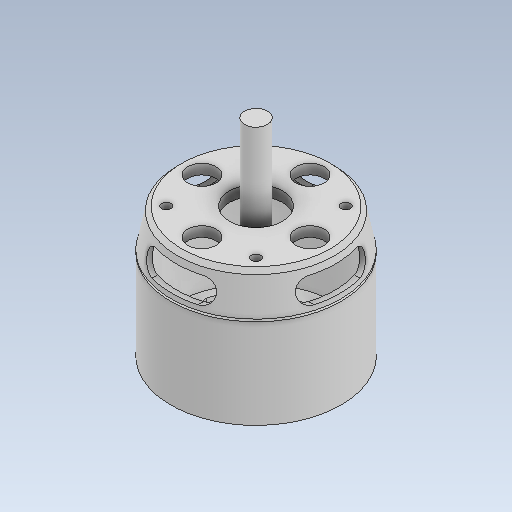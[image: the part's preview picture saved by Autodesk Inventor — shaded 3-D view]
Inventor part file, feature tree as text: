
AUTODESK INVENTOR PART (.ipt)
format: ipt  version: 2023 (Build 270158000, 158)  size: 352,768 bytes
history: native  units: in
note: dims shown in document units (in); Inventor stores cm internally (conversion verified against a paired STEP export)
features: extrude x4, sketch x4, pattern_circular x2, revolve x1, plane x1
ambient origin geometry x8: Origin, YZ Plane, XZ Plane, XY Plane, X Axis, Y Axis, Z Axis, Center Point
bodies: Solid1 (feature_tree)
feature tree (12):
  revolve  "Revolution1"  [1 undecoded]
  extrude  "Extrusion1"  Depth=0.5161in
  plane  "Work Plane1"
  extrude  "Extrusion2"  Depth=0.0787in
  sketch  "Sketch4"  dims[d6=45.0deg d7=0.3616in d8=0.0315in d9=1.2252in d10=0.1102in d11=0.1575in d12=3.2677in d13=1.0433in d14=0.0835in d16=0.0709in d17=0.1102in d18=0.3248in d19=0.6713in d20=90.0deg d21=0.3878in d22=0.128in d23=45.0deg d24=0.8661in d25=0.7382in d26=0.3937in d27=0.0in d28=1.1875in d29=0.315in d30=0.315in d31=0.2165in d32=0.6299in d33=0.3937in d34=0.0in d35=0.0906in d36=0.3937in d37=45.0deg d38=0.3937in d39=0.0in d40=1.5748in d41=360.0deg d43=0.9843in d44=2.0472in d46=0.3937in d47=0.0787in d48=0.3937in d49=0.0in d50=1.9685in d51=360.0deg]
  extrude  "Extrusion3"  Depth=0.3937in
  pattern_circular  "Circular Pattern1"  [2 undecoded]
  extrude  "Extrusion4"  Depth=0.3937in
  pattern_circular  "Circular Pattern2"  [2 undecoded]
  sketch  "Sketch1"  dims[d0=0.1378in d1=1.1614in]
  sketch  "Sketch2"  dims[d2=0.0709in d3=0.5161in]
  sketch  "Sketch3"  dims[d4=1.0573in d5=0.0787in]
note: 5 required parameter values undecoded (feature->parameter linkage not recoverable at this tier; creation-order binding heuristic only, values carry confidence <= 0.55)